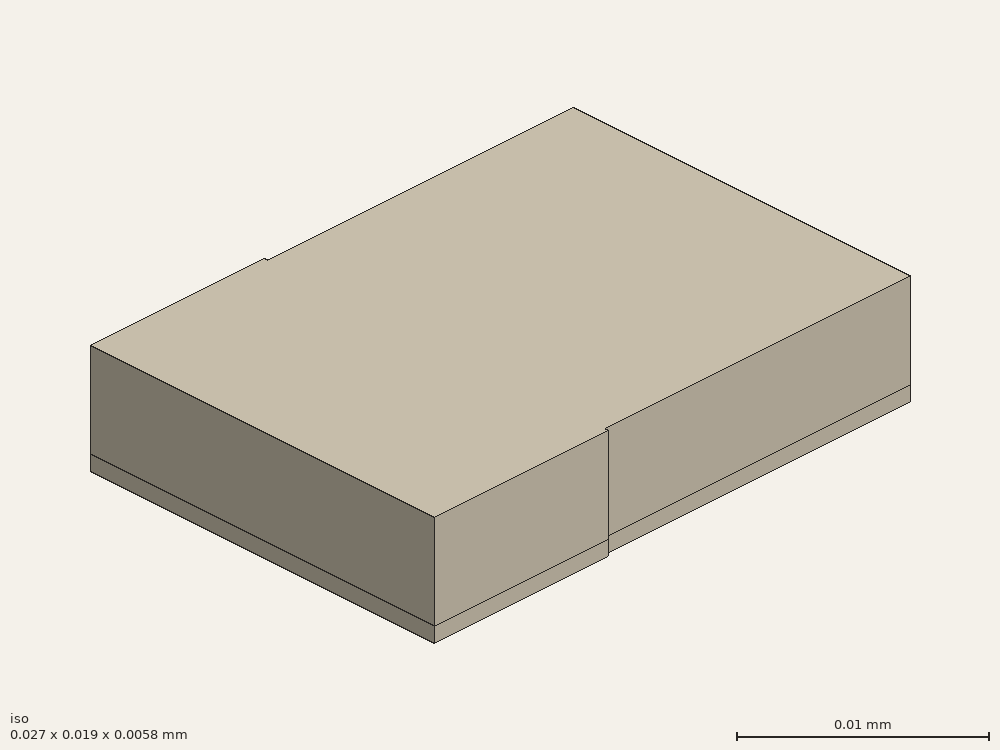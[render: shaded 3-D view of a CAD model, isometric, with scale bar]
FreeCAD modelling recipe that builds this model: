
FCSTD DOCUMENT  (FreeCAD 0.21R33694 (Git))
Label: filter
License: All rights reserved
LicenseURL: http://en.wikipedia.org/wiki/All_rights_reserved
objects: Part::Part2DObjectPython×41, Part::Extrusion×13, Part::Cut×5, App::FeaturePython×4, Part::FeaturePython×2, Part::MultiFuse×1
note: 62 computed .brp shape members not serialized (recipe doc carries the construction recipe); baked Part::Feature solids carry a one-line shape summary decoded from their .brp

FEATURE [Part::Part2DObjectPython] Rectangle  # Draft 2D object (typed FeaturePython)
  Area = 2.06
  ChamferSize = 0
  Columns = 1
  FilletRadius = 0
  Height = 0.2
  Length = 10.3
  MakeFace = true
  Placement = pos=(0,-0.1,0) rot=(0,0,1;0rad)
  Rows = 1
FEATURE [Part::Part2DObjectPython] Rectangle001  # Draft 2D object (typed FeaturePython)
  Area = 0.302
  ChamferSize = 0
  Columns = 1
  FilletRadius = 0
  Height = 1.51
  Length = 0.2
  MakeFace = true
  Placement = pos=(-0.2,0.1,0) rot=(0,0,1;0rad)
  Rows = 1
FEATURE [Part::Part2DObjectPython] Rectangle002  # Draft 2D object (typed FeaturePython)
  Area = 0.302
  ChamferSize = 0
  Columns = 1
  FilletRadius = 0
  Height = 1.51
  Length = 0.2
  MakeFace = true
  Placement = pos=(-0.2,-1.61,0) rot=(0,0,1;0rad)
  Rows = 1
FEATURE [Part::Part2DObjectPython] Rectangle003  # Draft 2D object (typed FeaturePython)
  Area = 3.678
  ChamferSize = 0
  Columns = 1
  FilletRadius = 0
  Height = 0.2
  Length = 18.39
  MakeFace = true
  Placement = pos=(-0.2,1.61,0) rot=(0,0,1;0rad)
  Rows = 1
FEATURE [Part::Part2DObjectPython] Rectangle004  # Draft 2D object (typed FeaturePython)
  Area = 3.678
  ChamferSize = 0
  Columns = 1
  FilletRadius = 0
  Height = 0.2
  Length = 18.39
  MakeFace = true
  Placement = pos=(-0.2,-1.81,0) rot=(0,0,1;0rad)
  Rows = 1
FEATURE [Part::Part2DObjectPython] Rectangle005  # Draft 2D object (typed FeaturePython)
  Area = 0.04
  ChamferSize = 0
  Columns = 1
  FilletRadius = 0
  Height = 0.2
  Length = 0.2
  MakeFace = true
  Placement = pos=(-0.2,-0.1,0) rot=(0,0,1;0rad)
  Rows = 1
FEATURE [Part::Part2DObjectPython] Rectangle008  # Draft 2D object (typed FeaturePython)
  Area = 3.742
  ChamferSize = 0
  Columns = 1
  FilletRadius = 0
  Height = 0.2
  Length = 18.71
  MakeFace = true
  Placement = pos=(-0.2,1.93,0) rot=(0,0,1;0rad)
  Rows = 1
FEATURE [Part::Part2DObjectPython] Rectangle009  # Draft 2D object (typed FeaturePython)
  Area = 3.742
  ChamferSize = 0
  Columns = 1
  FilletRadius = 0
  Height = 0.2
  Length = 18.71
  MakeFace = true
  Placement = pos=(-0.2,-2.13,0) rot=(0,0,1;0rad)
  Rows = 1
FEATURE [Part::Part2DObjectPython] Rectangle010  # Draft 2D object (typed FeaturePython)
  Area = 3.678
  ChamferSize = 0
  Columns = 1
  FilletRadius = 0
  Height = 0.2
  Length = 18.39
  MakeFace = true
  Placement = pos=(-0.2,2.25,0) rot=(0,0,1;0rad)
  Rows = 1
FEATURE [Part::Part2DObjectPython] Rectangle011  # Draft 2D object (typed FeaturePython)
  Area = 3.678
  ChamferSize = 0
  Columns = 1
  FilletRadius = 0
  Height = 0.2
  Length = 18.39
  MakeFace = true
  Placement = pos=(-0.2,-2.45,0) rot=(0,0,1;0rad)
  Rows = 1
FEATURE [Part::Part2DObjectPython] Rectangle012  # Draft 2D object (typed FeaturePython)
  Area = 1.78
  ChamferSize = 0
  Columns = 1
  FilletRadius = 0
  Height = 4.45
  Length = 0.4
  MakeFace = true
  Placement = pos=(18.51,2.13,0) rot=(0,0,1;0rad)
  Rows = 1
FEATURE [Part::Part2DObjectPython] Rectangle013  # Draft 2D object (typed FeaturePython)
  Area = 1.78
  ChamferSize = 0
  Columns = 1
  FilletRadius = 0
  Height = 4.45
  Length = 0.4
  MakeFace = true
  Placement = pos=(18.51,-6.58,0) rot=(0,0,1;0rad)
  Rows = 1
FEATURE [Part::Part2DObjectPython] Rectangle014  # Draft 2D object (typed FeaturePython)
  Area = 5.468
  ChamferSize = 0
  Columns = 1
  FilletRadius = 0
  Height = 0.4
  Length = 13.67
  MakeFace = true
  Placement = pos=(4.84,6.58,0) rot=(0,0,1;0rad)
  Rows = 1
FEATURE [Part::Part2DObjectPython] Rectangle015  # Draft 2D object (typed FeaturePython)
  Area = 5.468
  ChamferSize = 0
  Columns = 1
  FilletRadius = 0
  Height = 0.4
  Length = 13.67
  MakeFace = true
  Placement = pos=(4.84,-6.98,0) rot=(0,0,1;0rad)
  Rows = 1
FEATURE [Part::Part2DObjectPython] Rectangle016  # Draft 2D object (typed FeaturePython)
  Area = 0.16
  ChamferSize = 0
  Columns = 1
  FilletRadius = 0
  Height = 0.4
  Length = 0.4
  MakeFace = true
  Placement = pos=(18.51,6.58,0) rot=(0,0,1;0rad)
  Rows = 1
FEATURE [Part::Part2DObjectPython] Rectangle017  # Draft 2D object (typed FeaturePython)
  Area = 0.16
  ChamferSize = 0
  Columns = 1
  FilletRadius = 0
  Height = 0.4
  Length = 0.4
  MakeFace = true
  Placement = pos=(18.51,-6.98,0) rot=(0,0,1;0rad)
  Rows = 1
FEATURE [Part::Part2DObjectPython] Rectangle018  # Draft 2D object (typed FeaturePython)
  Area = 0.08
  ChamferSize = 0
  Columns = 1
  FilletRadius = 0
  Height = 0.2
  Length = 0.4
  MakeFace = true
  Placement = pos=(18.51,-2.13,0) rot=(0,0,1;0rad)
  Rows = 1
FEATURE [Part::Part2DObjectPython] Rectangle019  # Draft 2D object (typed FeaturePython)
  Area = 0.08
  ChamferSize = 0
  Columns = 1
  FilletRadius = 0
  Height = 0.2
  Length = 0.4
  MakeFace = true
  Placement = pos=(18.51,1.93,0) rot=(0,0,1;0rad)
  Rows = 1
FEATURE [Part::Part2DObjectPython] Rectangle020  # Draft 2D object (typed FeaturePython)
  Area = 0.127
  ChamferSize = 0
  Columns = 1
  FilletRadius = 0
  Height = 0.2
  Length = 0.635
  MakeFace = true
  Placement = pos=(-0.835,2.25,0) rot=(0,0,1;0rad)
  Rows = 1
FEATURE [Part::Part2DObjectPython] Rectangle021  # Draft 2D object (typed FeaturePython)
  Area = 0.127
  ChamferSize = 0
  Columns = 1
  FilletRadius = 0
  Height = 0.2
  Length = 0.635
  MakeFace = true
  Placement = pos=(-0.835,-2.45,0) rot=(0,0,1;0rad)
  Rows = 1
FEATURE [Part::Part2DObjectPython] Rectangle023  # Draft 2D object (typed FeaturePython)
  Area = 6.195
  ChamferSize = 0
  Columns = 1
  FilletRadius = 0
  Height = 3.5
  Length = 1.77
  MakeFace = true
  Placement = pos=(-1.4025,4.44,0) rot=(0,0,1;0rad)
  Rows = 1
FEATURE [Part::Part2DObjectPython] Wire  # Draft 2D object (typed FeaturePython)
  Area = 2.39297
  ChamferSize = 0
  Closed = true
  End = (-0.2,2.45,0)
  FilletRadius = 0
  Length = 6.54367
  MakeFace = true
  Placement = pos=(-0.835,2.45,0) rot=(0,0,1;0rad)
  Points = (4) [(0,0,0),(-0.5675,1.99,0),(1.2025,1.99,0),(0.635,0,0)]
  Start = (-0.835,2.45,0)
  Subdivisions = 0
FEATURE [Part::Part2DObjectPython] Rectangle025  # Draft 2D object (typed FeaturePython)
  Area = 6.195
  ChamferSize = 0
  Columns = 1
  FilletRadius = 0
  Height = 3.5
  Length = 1.77
  MakeFace = true
  Placement = pos=(-1.4025,-7.94,0) rot=(0,0,1;0rad)
  Rows = 1
FEATURE [Part::Part2DObjectPython] Wire001  # Draft 2D object (typed FeaturePython)
  Area = 2.39297
  ChamferSize = 0
  Closed = true
  End = (-0.2,-2.45,0)
  FilletRadius = 0
  Length = 6.54367
  MakeFace = true
  Placement = pos=(-0.835,-2.45,0) rot=(0,0,1;0rad)
  Points = (4) [(0,0,0),(-0.5675,-1.99,0),(1.2025,-1.99,0),(0.635,0,0)]
  Start = (-0.835,-2.45,0)
  Subdivisions = 0
FEATURE [Part::Part2DObjectPython] Wire002  # Draft 2D object (typed FeaturePython)
  Area = 12.393
  ChamferSize = 0
  Closed = true
  End = (0.3675,7.94,0)
  FilletRadius = 0
  Length = 50.7237
  MakeFace = true
  Placement = pos=(-1.4025,7.94,0) rot=(0,0,1;0rad)
  Points = (9) [(0,0,0),(0,-3.5,0),(0.5675,-5.49,0),(0.5675,-5.69,0),(19.5925,-5.69,0),(19.5925,-5.49,0),(1.2025,-5.49,0),(1.77,-3.5,0),(1.77,0,0)]
  Start = (-1.4025,7.94,0)
  Subdivisions = 0
FEATURE [Part::Part2DObjectPython] Wire003  # Draft 2D object (typed FeaturePython)
  Area = 11.23
  ChamferSize = 0
  Closed = true
  End = (-0.2,2.13,0)
  FilletRadius = 0
  Length = 75.66
  MakeFace = true
  Placement = pos=(-0.2,1.93,0) rot=(0,0,1;0rad)
  Points = (8) [(0,0,0),(19.11,-2.22045e-16,0),(19.11,5.05,0),(5.04,5.05,0),(5.04,4.65,0),(18.71,4.65,0),(18.71,0.2,0),(0,0.2,0)]
  Start = (-0.2,1.93,0)
  Subdivisions = 0
FEATURE [Part::Part2DObjectPython] Wire004  # Draft 2D object (typed FeaturePython)
  Area = 10.06
  ChamferSize = 0
  Closed = true
  End = (18.19,1.61,0)
  FilletRadius = 0
  Length = 101
  MakeFace = true
  Placement = pos=(18.19,1.81,0) rot=(0,0,1;0rad)
  Points = (12) [(0,0,0),(-18.39,0,0),(-18.39,-3.62,0),(0,-3.62,0),(0,-3.42,0),(-18.19,-3.42,0),(-18.19,-1.91,0),(-7.89,-1.91,0),(-7.89,-1.71,0),(-18.19,-1.71,0),(-18.19,-0.2,0),(0,-0.2,0)]
  Start = (18.19,1.81,0)
  Subdivisions = 0
FEATURE [Part::Part2DObjectPython] Wire005  # Draft 2D object (typed FeaturePython)
  Area = 11.23
  ChamferSize = 0
  Closed = true
  End = (-0.2,-1.93,0)
  FilletRadius = 0
  Length = 75.66
  MakeFace = true
  Placement = pos=(-0.2,-2.13,0) rot=(0,0,1;0rad)
  Points = (8) [(0,0,0),(18.71,0,0),(18.71,-4.45,0),(5.04,-4.45,0),(5.04,-4.85,0),(19.11,-4.85,0),(19.11,0.2,0),(0,0.2,0)]
  Start = (-0.2,-2.13,0)
  Subdivisions = 0
FEATURE [Part::Part2DObjectPython] Wire006  # Draft 2D object (typed FeaturePython)
  Area = 12.393
  ChamferSize = 0
  Closed = true
  End = (-1.4025,-4.44,0)
  FilletRadius = 0
  Length = 50.7237
  MakeFace = true
  Placement = pos=(-1.4025,-7.94,0) rot=(0,0,1;0rad)
  Points = (9) [(0,0,0),(1.77,0,0),(1.77,3.5,0),(1.2025,5.49,0),(19.5925,5.49,0),(19.5925,5.69,0),(0.5675,5.69,0),(0.5675,5.49,0),(0,3.5,0)]
  Start = (-1.4025,-7.94,0)
  Subdivisions = 0
FEATURE [Part::Part2DObjectPython] Rectangle026  # Draft 2D object (typed FeaturePython)
  Area = 3.1329
  ChamferSize = 0
  Columns = 1
  FilletRadius = 0
  Height = 1.77
  Length = 1.77
  MakeFace = true
  Placement = pos=(-1.4025,7.94,0) rot=(0,0,1;0rad)
  Rows = 1
FEATURE [Part::Part2DObjectPython] Rectangle027  # Draft 2D object (typed FeaturePython)
  Area = 3.1329
  ChamferSize = 0
  Columns = 1
  FilletRadius = 0
  Height = 1.77
  Length = 1.77
  MakeFace = true
  Placement = pos=(-1.4025,-9.71,0) rot=(0,0,1;0rad)
  Rows = 1
FEATURE [Part::Part2DObjectPython] Rectangle028  # Draft 2D object (typed FeaturePython)
  Area = 524.34
  ChamferSize = 0
  Columns = 1
  FilletRadius = 0
  Height = 19.42
  Length = 27
  MakeFace = true
  Placement = pos=(-5.4025,-9.71,0) rot=(0,0,1;0rad)
  Rows = 1
FEATURE [Part::Extrusion] Extrude  label="RO4003C"
  Base = -> Rectangle028
  Dir = (0,0,1)
  DirMode = 2
  FaceMakerClass = Part::FaceMakerBullseye
  LengthFwd = 0
  LengthRev = 0.813
  Solid = false
  Symmetric = false
FEATURE [Part::Part2DObjectPython] Rectangle029  # Draft 2D object (typed FeaturePython)
  Area = 524.34
  ChamferSize = 0
  Columns = 1
  FilletRadius = 0
  Height = 19.42
  Length = 27
  MakeFace = true
  Placement = pos=(-5.4025,-9.71,0) rot=(0,0,1;0rad)
  Rows = 1
FEATURE [Part::Extrusion] Extrude001  label="air"
  Base = -> Rectangle029
  Dir = (0,0,1)
  DirMode = 2
  FaceMakerClass = Part::FaceMakerBullseye
  LengthFwd = 5
  LengthRev = 0
  Solid = false
  Symmetric = false
FEATURE [Part::Extrusion] Extrude002
  Base = -> Wire002
  Dir = (0,0,1)
  DirMode = 2
  FaceMakerClass = Part::FaceMakerBullseye
  LengthFwd = 0.015
  LengthRev = 0
  Solid = false
  Symmetric = false
FEATURE [Part::Extrusion] Extrude004
  Base = -> Wire003
  Dir = (0,0,1)
  DirMode = 2
  FaceMakerClass = Part::FaceMakerBullseye
  LengthFwd = 0.015
  LengthRev = 0
  Solid = false
  Symmetric = false
FEATURE [Part::Extrusion] Extrude005
  Base = -> Wire004
  Dir = (0,0,1)
  DirMode = 2
  FaceMakerClass = Part::FaceMakerBullseye
  LengthFwd = 0.015
  LengthRev = 0
  Solid = false
  Symmetric = false
FEATURE [Part::Extrusion] Extrude006
  Base = -> Wire005
  Dir = (0,0,1)
  DirMode = 2
  FaceMakerClass = Part::FaceMakerBullseye
  LengthFwd = 0.015
  LengthRev = 0
  Solid = false
  Symmetric = false
FEATURE [Part::Extrusion] Extrude007
  Base = -> Wire006
  Dir = (0,0,1)
  DirMode = 2
  FaceMakerClass = Part::FaceMakerBullseye
  LengthFwd = 0.015
  LengthRev = 0
  Solid = false
  Symmetric = false
FEATURE [Part::Extrusion] Extrude008
  Base = -> Rectangle026
  Dir = (0,0,1)
  DirMode = 2
  FaceMakerClass = Part::FaceMakerBullseye
  LengthFwd = 0.015
  LengthRev = 0
  Solid = false
  Symmetric = false
FEATURE [Part::Extrusion] Extrude010
  Base = -> Rectangle027
  Dir = (0,0,1)
  DirMode = 2
  FaceMakerClass = Part::FaceMakerBullseye
  LengthFwd = 0.015
  LengthRev = 0
  Solid = false
  Symmetric = false
FEATURE [Part::MultiFuse] Fusion  label="metal"
  Shapes = -> [Extrude002,Extrude004,Extrude005,Extrude006,Extrude007,Extrude008,Extrude010]
FEATURE [Part::Cut] Cut  label="air_metal"
  Base = -> Extrude001
  Tool = -> Fusion
FEATURE [Part::Part2DObjectPython] Line  label="_PV1"  # Draft 2D object (typed FeaturePython)
  Area = 0
  ChamferSize = 0
  Closed = false
  End = (-0.0005175,-0.00971,-0.000813)
  FilletRadius = 0
  Length = 0.000813
  MakeFace = true
  Placement = pos=(-0.0005175,-0.00971,0) rot=(1,0,0;1.5708rad)
  Points = (2) [(0,0,0),(0,-0.000813,0)]
  Start = (-0.0005175,-0.00971,0)
  Subdivisions = 0
FEATURE [Part::Part2DObjectPython] Line001  label="_PV2"  # Draft 2D object (typed FeaturePython)
  Area = 0
  ChamferSize = 0
  Closed = false
  End = (-0.0005175,0.00971,-0.000813)
  FilletRadius = 0
  Length = 0.000813
  MakeFace = true
  Placement = pos=(-0.0005175,0.00971,0) rot=(-1,0,0;1.5708rad)
  Points = (2) [(0,0,0),(0,0.000813,0)]
  Start = (-0.0005175,0.00971,0)
  Subdivisions = 0
FEATURE [App::FeaturePython] Text  label="_S1(PV){port1}"  # WARN: FeaturePython — macro-defined, semantics opaque (R4)
  Placement = pos=(-0.0362145,0.00971,-0.0339181) rot=(-1,0,0;1.5708rad)
  Text = .
FEATURE [App::FeaturePython] Text001  label="_S2(PV){port2}"  # WARN: FeaturePython — macro-defined, semantics opaque (R4)
  Placement = pos=(-0.0362145,0.00971,-0.0339181) rot=(-1,0,0;1.5708rad)
  Text = .
FEATURE [App::FeaturePython] Text002  label="_L1(1,voltage){V1}"  # WARN: FeaturePython — macro-defined, semantics opaque (R4)
  Placement = pos=(-0.0362145,0.00971,-0.0339181) rot=(-1,0,0;1.5708rad)
  Text = .
FEATURE [App::FeaturePython] Text003  label="_L2(2,voltage){V2}"  # WARN: FeaturePython — macro-defined, semantics opaque (R4)
  Placement = pos=(-0.0362145,0.00971,-0.0339181) rot=(-1,0,0;1.5708rad)
  Text = .
FEATURE [Part::Part2DObjectPython] Rectangle033  # Draft 2D object (typed FeaturePython)
  Area = 14.008
  ChamferSize = 0
  Columns = 1
  FilletRadius = 0
  Height = 0.813
  Length = 17.23
  MakeFace = true
  Placement = pos=(4.3675,-9.71,-0.813) rot=(1,0,0;1.5708rad)
  Rows = 1
FEATURE [Part::Part2DObjectPython] Rectangle034  # Draft 2D object (typed FeaturePython)
  Area = 86.15
  ChamferSize = 0
  Columns = 1
  FilletRadius = 0
  Height = 5
  Length = 17.23
  MakeFace = true
  Placement = pos=(4.3675,-9.71,0) rot=(1,0,0;1.5708rad)
  Rows = 1
FEATURE [Part::Extrusion] Extrude011
  Base = -> Rectangle033
  Dir = (0,-1,2e-16)
  DirMode = 2
  FaceMakerClass = Part::FaceMakerBullseye
  LengthFwd = 0
  LengthRev = 0.2
  Solid = false
  Symmetric = false
FEATURE [Part::Extrusion] Extrude012
  Base = -> Rectangle034
  Dir = (0,-1,2e-16)
  DirMode = 2
  FaceMakerClass = Part::FaceMakerBullseye
  LengthFwd = 0
  LengthRev = 0.2
  Solid = false
  Symmetric = false
FEATURE [Part::Cut] Cut001
  Base = -> Extrude
  Tool = -> Extrude011
FEATURE [Part::Cut] Cut002
  Base = -> Cut
  Tool = -> Extrude012
FEATURE [Part::Part2DObjectPython] Rectangle037  # Draft 2D object (typed FeaturePython)
  Area = 14.008
  ChamferSize = 0
  Columns = 1
  FilletRadius = 0
  Height = 0.813
  Length = 17.23
  MakeFace = true
  Placement = pos=(4.3675,9.71,0) rot=(-1,0,0;1.5708rad)
  Rows = 1
FEATURE [Part::Part2DObjectPython] Rectangle038  # Draft 2D object (typed FeaturePython)
  Area = 86.15
  ChamferSize = 0
  Columns = 1
  FilletRadius = 0
  Height = 5
  Length = 17.23
  MakeFace = true
  Placement = pos=(4.3675,9.71,5) rot=(-1,0,0;1.5708rad)
  Rows = 1
FEATURE [Part::Extrusion] Extrude013
  Base = -> Rectangle037
  Dir = (0,1,2e-16)
  DirMode = 2
  FaceMakerClass = Part::FaceMakerBullseye
  LengthFwd = 0
  LengthRev = 0.2
  Solid = false
  Symmetric = false
FEATURE [Part::Cut] Cut003
  Base = -> Cut001
  Tool = -> Extrude013
FEATURE [Part::Extrusion] Extrude014
  Base = -> Rectangle038
  Dir = (0,1,2e-16)
  DirMode = 2
  FaceMakerClass = Part::FaceMakerBullseye
  LengthFwd = 0
  LengthRev = 0.2
  Solid = false
  Symmetric = false
FEATURE [Part::Cut] Cut004
  Base = -> Cut002
  Tool = -> Extrude014
FEATURE [Part::FeaturePython] BooleanFragments  # WARN: FeaturePython — macro-defined, semantics opaque (R4)
  Mode = 0
  Objects = -> [Cut003,Cut004]
  Tolerance = 0
FEATURE [Part::FeaturePython] Clone  label="scaled"  # Draft clone (typed FeaturePython)
  AttacherType = Attacher::AttachEngine3D
  Fuse = false
  Objects = -> [BooleanFragments]
  Scale = (0.001,0.001,0.001)
FEATURE [Part::Part2DObjectPython] Rectangle039  label="_Pport1"  # Draft 2D object (typed FeaturePython)
  Area = 5.6793e-05
  ChamferSize = 0
  Columns = 1
  FilletRadius = 0
  Height = 0.005813
  Length = 0.00977
  MakeFace = true
  Placement = pos=(-0.0054025,-0.00971,0.005) rot=(-1,0,0;1.5708rad)
  Rows = 1
FEATURE [Part::Part2DObjectPython] Rectangle040  label="_Pport2"  # Draft 2D object (typed FeaturePython)
  Area = 5.6793e-05
  ChamferSize = 0
  Columns = 1
  FilletRadius = 0
  Height = 0.005813
  Length = 0.00977
  MakeFace = true
  Placement = pos=(-0.0054025,0.00971,0.005) rot=(-1,0,0;1.5708rad)
  Rows = 1
